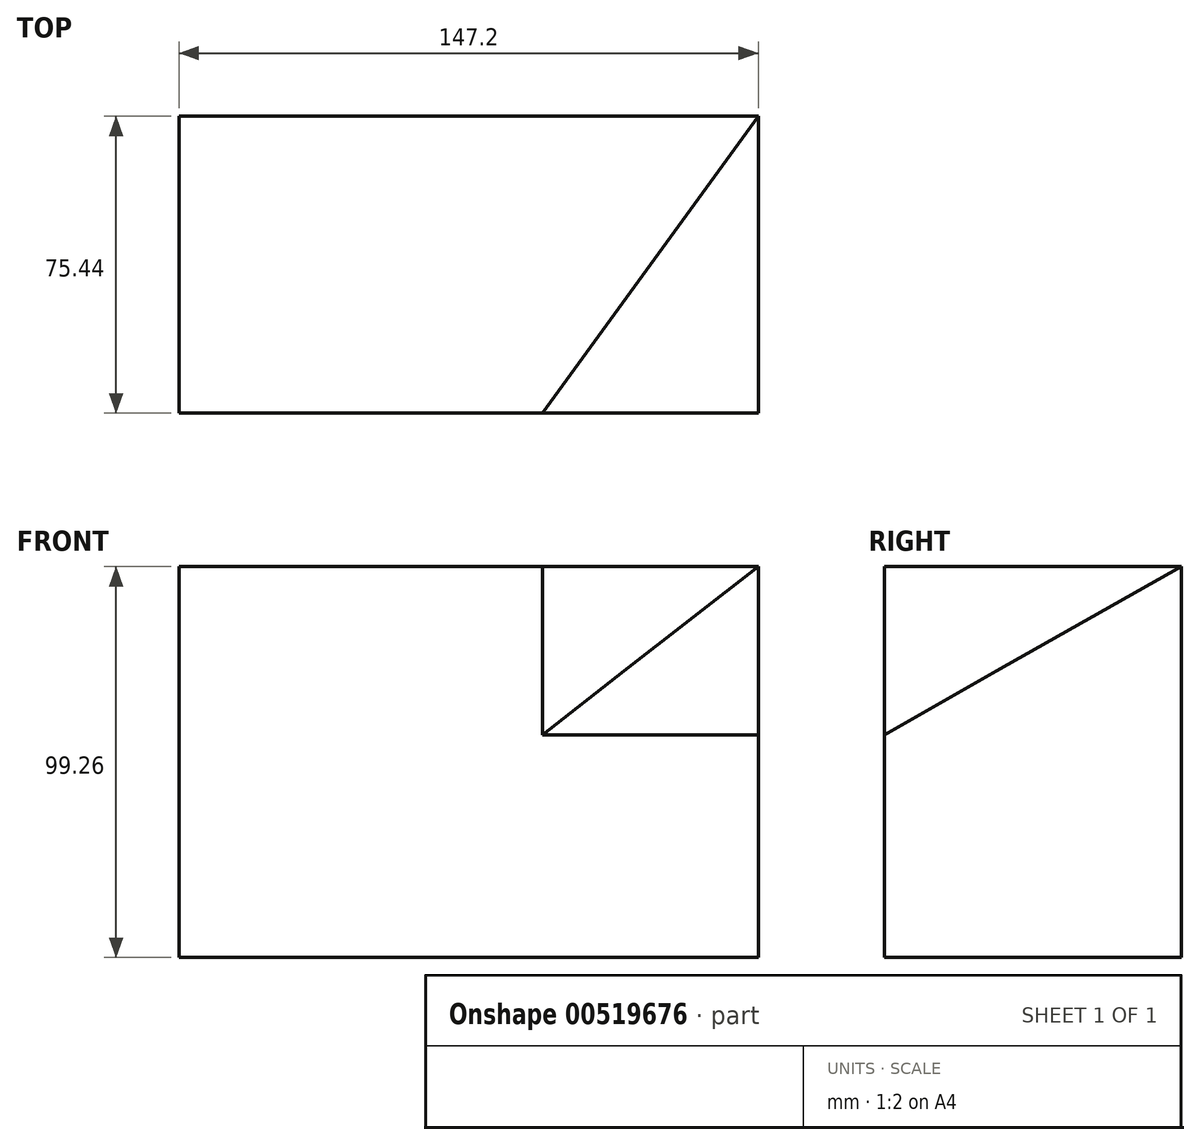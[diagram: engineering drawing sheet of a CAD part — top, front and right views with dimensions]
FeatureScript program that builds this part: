
annotation { "Feature Type Name" : "Feature", "Feature Type Description" : "" }
export const myFeature = defineFeature(function(context is Context, id is Id, definition is map)
    precondition{}
    {
        {
            var Q0;
            Q0=qCreatedBy(makeId("Front.planeOp"),FACE);
            var sketch = newSketch(context, id + "F0", { "sketchPlane" : qUnion([Q0])});
            skLineSegment(sketch, "E0.bottom", {"start": v(-60.52, 24.24) * mm, "end": v(86.68, 24.24) * mm});
            skLineSegment(sketch, "E0.top", {"start": v(-60.52, -75.02) * mm, "end": v(86.68, -75.02) * mm});
            skLineSegment(sketch, "E0.left", {"start": v(-60.52, 24.24) * mm, "end": v(-60.52, -75.02) * mm});
            skLineSegment(sketch, "E0.right", {"start": v(86.68, 24.24) * mm, "end": v(86.68, -75.02) * mm});
            skSolve(sketch);
        }
        {
            var Q0;
            Q0 = qSketchRegion(id + "F0", true);
            extrude(context, id + "F1", {"entities" : qUnion([Q0]), "depth" : 75.44 * mm, "offsetDistance" : 25.4 * mm});
        }
        {
            var Q0;
            Q0=makeQuery(id+"F1.opExtrude","SWEPT_FACE",FACE,{"disambiguationData":[OSD([sQuery(id+"F0.wireOp",EDGE,"E0.bottom")])]});
            var sketch = newSketch(context, id + "F2", { "sketchPlane" : qUnion([Q0])});
            skLineSegment(sketch, "E1", {"start": v(86.68, 0) * mm, "end": v(31.86, -75.44) * mm});
            skLineSegment(sketch, "E2", {"start": v(31.86, -75.44) * mm, "end": v(86.68, -75.44) * mm});
            skLineSegment(sketch, "E3", {"start": v(86.68, -75.44) * mm, "end": v(86.68, 0) * mm});
            skSolve(sketch);
        }
        {
            var Q0;
            Q0=makeQuery(id+"F1.opExtrude","SWEPT_FACE",FACE,{"disambiguationData":[OSD([sQuery(id+"F0.wireOp",EDGE,"E0.right")])]});
            var sketch = newSketch(context, id + "F3", { "sketchPlane" : qUnion([Q0])});
            skLineSegment(sketch, "E4", {"start": v(0, 24.24) * mm, "end": v(-75.44, -18.27) * mm});
            skLineSegment(sketch, "E5", {"start": v(-75.44, -18.27) * mm, "end": v(-75.44, 24.24) * mm});
            skLineSegment(sketch, "E6", {"start": v(-75.44, 24.24) * mm, "end": v(0, 24.24) * mm});
            skSolve(sketch);
        }
        {
            var Q0;
            Q0=makeQuery(id+"F2.imprint","IMPRINT",FACE,{"disambiguationData":[TD([[makeQuery(id+"F2.imprint","IMPRINT",EDGE,{"derivedFrom":sQuery(id+"F2.wireOp",EDGE,"E1")}),1.0]])]});
            extrude(context, id + "F4", {"entities" : qUnion([Q0]), "operationType" : NewBodyOperationType.REMOVE, "oppositeDirection" : true, "depth" : 44.7 * mm, "offsetDistance" : 25.4 * mm});
        }
        {
            var Q0;
            {var subQ0=sQuery(id+"F3.wireOp",EDGE,"E4");Q0=makeQuery(id+"F3.imprint","IMPRINT",FACE,{"disambiguationData":[TD([[makeQuery(id+"F3.imprint","IMPRINT",EDGE,{"derivedFrom":subQ0}),1.0]])]});}
            var sketch = newSketch(context, id + "F5", { "sketchPlane" : qUnion([Q0])});
            skLineSegment(sketch, "E7", {"start": v(-75.69, -18.65) * mm, "end": v(-75.69, -23.97) * mm});
            skLineSegment(sketch, "E8", {"start": v(-75.69, -23.97) * mm, "end": v(0, -23.97) * mm});
            skLineSegment(sketch, "E9", {"start": v(0, -23.97) * mm, "end": v(0, 24.63) * mm});
            skLineSegment(sketch, "E10", {"start": v(0, 24.63) * mm, "end": v(-75.69, -18.65) * mm});
            skSolve(sketch);
        }
        {
            var Q0;
            {var subQ0=sQuery(id+"F5.wireOp",EDGE,"E9");var subQ1=sQuery(id+"F3.wireOp",EDGE,"E4");var subQ2=makeQuery(id+"F3.imprint","IMPRINT",EDGE,{"derivedFrom":subQ1});var subQ3=makeQuery(id+"F5.imprint","INTERSECT",VERTEX,{"derivedFrom":[subQ2,subQ0]});Q0=makeQuery(id+"F5.imprint","IMPRINT",FACE,{"disambiguationData":[TD([[makeQuery(id+"F5.imprint","IMPRINT",EDGE,{"disambiguationData":[TD([[subQ3,-1.0]])],"derivedFrom":subQ2}),1.0]])]});}
            extrude(context, id + "F6", {"entities" : qUnion([Q0]), "operationType" : NewBodyOperationType.ADD, "oppositeDirection" : true, "depth" : 65.28 * mm, "offsetDistance" : 25.4 * mm});
        }
    });
